# Revit family: Hutprofil 45-45, VA
name_source: partatom
category: HLS-Bauteile
revit_build: Autodesk Revit 2017 (Build: 20190507_1515(x64)
units: mm (PartAtom-declared; Revit-internal decimal feet)

## family parameters
Arbeitsebenenbasiert = Ja
Beim Laden mit Abzugskörper schneiden = Nein
Bemaßung runder Anschluss = Durchmesser verwenden
Gemeinsam genutzt = Ja
Immer vertikal = Nein
Raumberechnungspunkt = Nein
Teiletyp = Normal

## types (1)
- Hutprofil 45-45, V4A
    Anschlusslochung = 13 mm
    Artikelnummer = 0481626
    Breite Material = 35 mm
    Fabrikat = MEFA
    Firma = MEFA Befestigungs- und Montagesysteme GmbH
    Gewicht = 0.23 kg
    Gewicht pro Bauteil = 0.23 kg
    H = 45 mm  [stored 0.147638 ft]
    Höhe = 45 mm
    Kurztext1 = Hutprofil C-Profil 45/45
    Kurztext2 = Höhe 45 mm Langloch
    Lochabstand = 105 mm
    Lochdurchmesser = 13 mm
    Länge = 134 mm
    Länge Innen = 46 mm
    Material = Edelstahl
    Materialname = V4A
    Profiltyp = 45/45
    Stärke Material = 4 mm  [stored 0.0131234 ft]
    Vorgabe-Ansicht = 1219 mm
    max. zul. Last = 3.50 kN

note: [stored X ft] marks values corroborated as IEEE doubles in the binary element streams (Revit-internal decimal feet)
